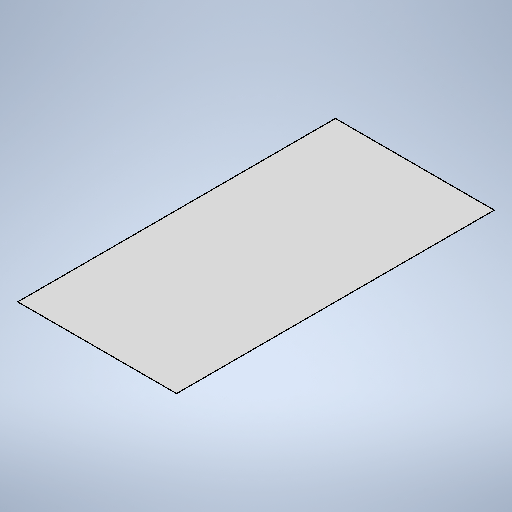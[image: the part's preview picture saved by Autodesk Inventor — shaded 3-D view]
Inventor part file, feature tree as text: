
AUTODESK INVENTOR PART (.ipt)
format: ipt  version: 2025 (Build 290162010, 162A)  size: 274,944 bytes
history: native  units: mm
features: other x2, sheet_metal_op x1, sketch x1
ambient origin geometry x8: Origin, YZ Plane, XZ Plane, XY Plane, X Axis, Y Axis, Z Axis, Center Point
bodies: Body1 (feature_tree)
feature tree (4):
  sheet_metal_op  "Face3"
  sketch  "Sketch1"  dims[d61=500.0mm d154=1250.0mm d155=2500.0mm d156=2.0mm]
  other  "Plate5"
  other  "Definition1"
